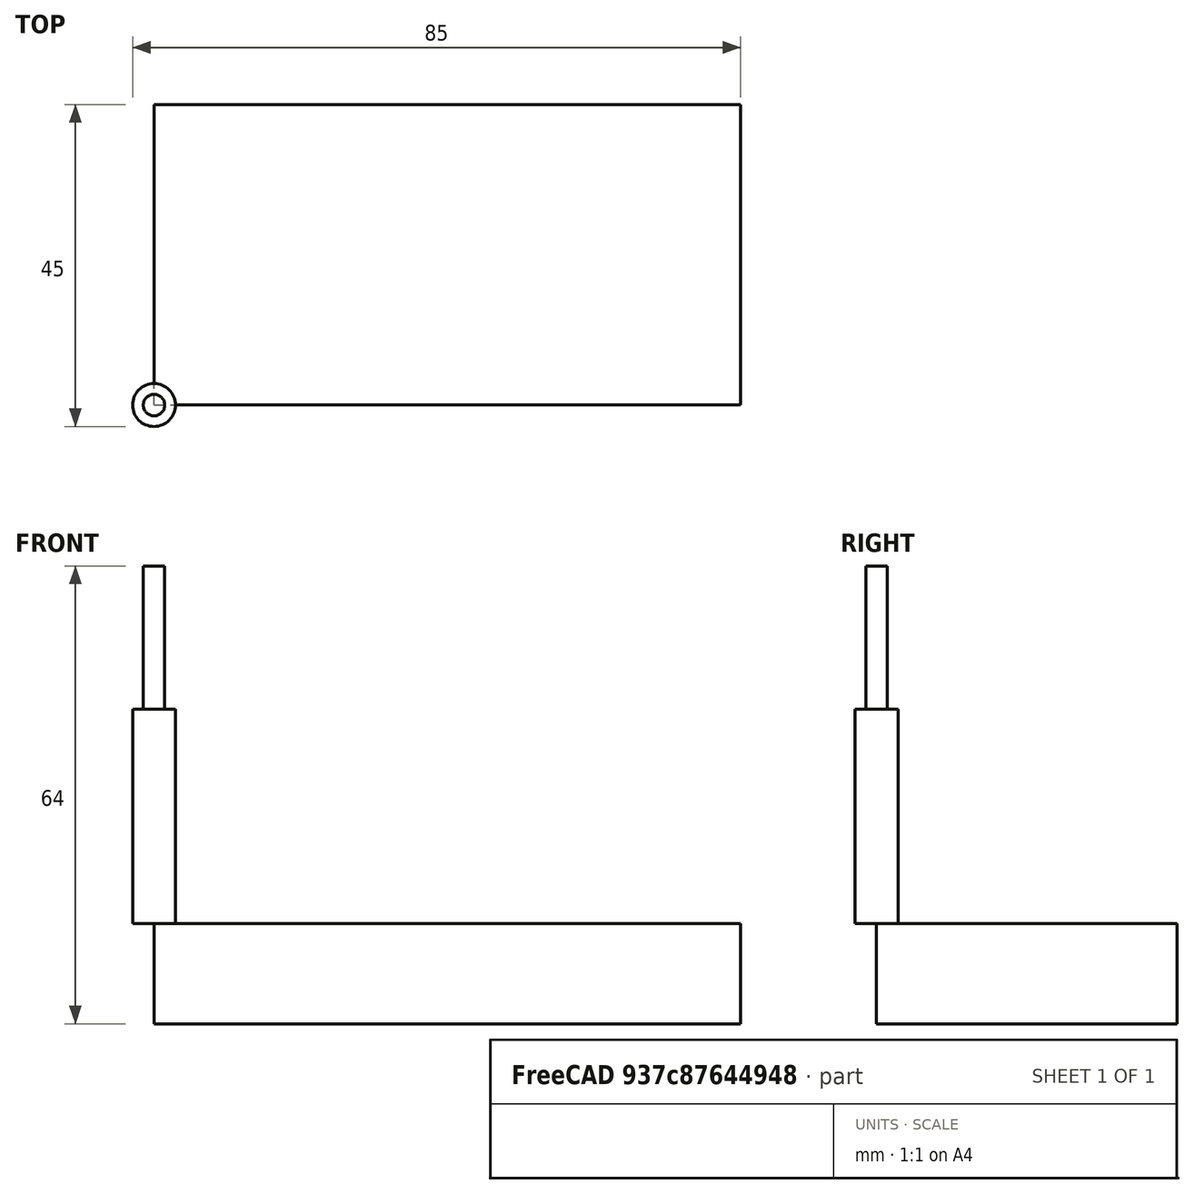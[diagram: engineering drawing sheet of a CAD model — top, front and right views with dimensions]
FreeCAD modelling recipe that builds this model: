
FCSTD DOCUMENT  (FreeCAD 0.19R23546 (Git))
Label: Cylindres
License: All rights reserved
LicenseURL: http://en.wikipedia.org/wiki/All_rights_reserved
objects: Path::FeaturePython×5, Sketcher::SketchObject×3, Part::FeaturePython×3, PartDesign::Pocket×2, PartDesign::Pad×1, App::FeaturePython×1, PartDesign::Body×1, App::DocumentObjectGroup×1, Path::FeatureCompoundPython×1, Mesh::FeaturePython×1
note: 15 computed .brp shape members not serialized (recipe doc carries the construction recipe); baked Part::Feature solids carry a one-line shape summary decoded from their .brp

FEATURE [Sketcher::SketchObject] Sketch
  MapMode = 5
  Support = -> [XY_Plane]
  sketch-geometry (4):
    g0: LineSegment StartX=0 StartY=40 StartZ=0 EndX=80 EndY=40 EndZ=0
    g1: LineSegment StartX=80 StartY=40 StartZ=0 EndX=80 EndY=0 EndZ=0
    g2: LineSegment StartX=80 StartY=0 StartZ=0 EndX=0 EndY=0 EndZ=0
    g3: LineSegment StartX=0 StartY=0 StartZ=0 EndX=0 EndY=40 EndZ=0
  constraints (9):
    c: Coincident(g0,g1)
    c: Coincident(g1,g2)
    c: Coincident(g2,g3)
    c: Coincident(g3,g0)
    c: Horizontal(g0)
    c: Horizontal(g2)
    c: Vertical(g1)
    c: Vertical(g3)
    c: PointOnObject(g0,g-2)
FEATURE [PartDesign::Pad] Pad
  Direction = (1,1,1)
  Length = 14
  Length2 = 100
  Profile = -> Sketch
  Type = 0
FEATURE [Sketcher::SketchObject] Sketch001
  MapMode = 5
  Placement = pos=(0,0,14) rot=(0,0,1;0rad)
  Support = -> [Pad]
  sketch-geometry (1):
    g0: Circle CenterX=20 CenterY=20 CenterZ=0 NormalX=0 NormalY=0 NormalZ=1 AngleXU=0 Radius=12.5
  constraints (1):
    c: Diameter(g0) = 25
FEATURE [PartDesign::Pocket] Pocket  label="Cylindre"
  BaseFeature = -> Pad
  Length = 5
  Length2 = 100
  Profile = -> Sketch001
  Type = 1
FEATURE [App::FeaturePython] SetupSheet  # Path/CAM operation (typed FeaturePython)
  ClearanceHeightExpression = OpStockZMax+SetupSheet.ClearanceHeightOffset
  ClearanceHeightOffset = 5
  CoolantMode = 0
  CoolantModes = None | Flood | Mist
  FinalDepthExpression = OpFinalDepth
  HorizRapid = 0
  SafeHeightExpression = OpStockZMax+SetupSheet.SafeHeightOffset
  SafeHeightOffset = 3
  StartDepthExpression = OpStartDepth
  StepDownExpression = OpToolDiameter
  VertRapid = 0
FEATURE [Part::FeaturePython] ToolBit  label="Endmill"  # Path/CAM toolbit (typed FeaturePython)
  BitShape = <path>
  CuttingEdgeHeight = 30
  Diameter = 6
  Length = 50
  ShankDiameter = 3
  ShapeName = endmill
FEATURE [Path::FeaturePython] TC__Default_Tool  label="TC: Default Tool"  # Path/CAM operation (typed FeaturePython)
  HorizFeed = 0
  HorizRapid = 0
  SpindleDir = 0
  SpindleSpeed = 0
  Tool = -> ToolBit
  ToolNumber = 1
  VertFeed = 0
  VertRapid = 0
  expr: HorizRapid = SetupSheet.HorizRapid
  expr: VertRapid = SetupSheet.VertRapid
FEATURE [Sketcher::SketchObject] Sketch002
  MapMode = 5
  Placement = pos=(0,0,14) rot=(0,0,1;0rad)
  Support = -> [Pocket]
  sketch-geometry (1):
    g0: Circle CenterX=60 CenterY=20 CenterZ=0 NormalX=0 NormalY=0 NormalZ=1 AngleXU=0 Radius=18.5
  constraints (1):
    c: Radius(g0) = 18.5
FEATURE [PartDesign::Pocket] Pocket001  label="Trou cylindrique"
  BaseFeature = -> Pocket
  Length = 5
  Length2 = 100
  Profile = -> Sketch002
  Type = 1
FEATURE [PartDesign::Body] Body
  Group = -> [Sketch,Pad,Sketch001,Pocket,Sketch002,Pocket001]
  Origin = -> Origin
  Tip = -> Pocket001
FEATURE [Part::FeaturePython] Clone  label="Model-Body"  # Draft clone (typed FeaturePython)
  AttacherType = Attacher::AttachEngine3D
  Fuse = false
  Objects = -> [Body]
  PathResource = Model
  Placement = pos=(1,1,-14) rot=(0,0,1;0rad)
  Scale = (1,1,1)
FEATURE [App::DocumentObjectGroup] Model
  Group = -> [Clone]
FEATURE [Part::FeaturePython] Stock  # WARN: FeaturePython — macro-defined, semantics opaque (R4)
  Base = -> Model
  ExtXneg = 1
  ExtXpos = 1
  ExtYneg = 1
  ExtYpos = 1
  ExtZneg = 0
  ExtZpos = 0
  Placement = pos=(1,1,-14) rot=(0,0,1;0rad)
  StockType = FromBase
FEATURE [Path::FeaturePython] Profile  # Path/CAM operation (typed FeaturePython)
  Active = true
  AreaParams:
    Tolerance = 1e-07
    FitArcs = True
    Simplify = False
    CleanDistance = 0.0
    Accuracy = 0.01
    Unit = 1.0
    MinArcPoints = 4
    MaxArcPoints = 100
    ClipperScale = 10000000.0
    Fill = 0
    Coplanar = 0
    Reorient = True
    Outline = False
    Explode = False
    OpenMode = 0
    Deflection = 0.01
    SubjectFill = 0
    ClipFill = 0
    Offset = -3.0
    ExtraPass = 0
    Stepover = 0.0
    LastStepover = 0.0
    JoinType = 0
    EndType = 0
    MiterLimit = 2.0
    RoundPrecision = 0.0
    PocketMode = 0
    ToolRadius = 1.0
    PocketExtraOffset = 0.0
    PocketStepover = 0.0
    PocketLastStepover = 0.0
    FromCenter = False
    Angle = 45.0
    AngleShift = 0.0
    Shift = 0.0
    Thicken = False
    SectionCount = -1
    Stepdown = 1.0
    SectionOffset = 0.0
    SectionTolerance = 1e-06
    SectionMode = 2
    Project = False
  AttemptInverseAngle = true
  Base = -> [Clone]
  ClearanceHeight = 5
  CoolantMode = None
  CycleTime = Erreur de temps de cycle
  Direction = 1
  EnableRotation = 0
  ExpandProfile = 0
  ExpandProfileStepOver = 100
  FinalDepth = -14
  HandleMultipleFeatures = 1
  InverseAngle = false
  JoinType = 0
  LimitDepthToFace = true
  MiterLimit = 0.1
  OffsetExtra = 0
  OpFinalDepth = -14
  OpStartDepth = 0
  OpStockZMax = 0
  OpStockZMin = -14
  OpToolDiameter = 6
  PathParams = {'orientation': 0, 'feedrate': 0.0, 'feedrate_v': 0.0, 'verbose': True, 'resume_height': 3.0, 'retraction': 5.0, 'return_end': True, 'preamble': False, 'start': Vector (0.0, 0.0, 0.0)}
  ReverseDirection = false
  SafeHeight = 3
  Side = 1
  StartDepth = 0
  StartPoint = (0,0,0)
  StepDown = 3
  ToolController = -> TC__Default_Tool
  UseComp = true
  UseStartPoint = true
  processCircles = false
  processHoles = false
  processPerimeter = true
  expr: ClearanceHeight = OpStockZMax + SetupSheet.ClearanceHeightOffset
  expr: SafeHeight = OpStockZMax + SetupSheet.SafeHeightOffset
  expr: StepDown = 3
  expr: FinalDepth = OpFinalDepth
  expr: StartDepth = OpStartDepth
FEATURE [Path::FeaturePython] Pocket_Shape  # Path/CAM operation (typed FeaturePython)
  Active = true
  AreaParams:
    Tolerance = 1e-07
    FitArcs = True
    Simplify = False
    CleanDistance = 0.0
    Accuracy = 0.01
    Unit = 1.0
    MinArcPoints = 4
    MaxArcPoints = 100
    ClipperScale = 10000000.0
    Fill = 0
    Coplanar = 0
    Reorient = True
    Outline = False
    Explode = False
    OpenMode = 0
    Deflection = 0.01
    SubjectFill = 0
    ClipFill = 0
    Offset = 0.0
    ExtraPass = 0
    Stepover = 0.0
    LastStepover = 0.0
    JoinType = 0
    EndType = 0
    MiterLimit = 2.0
    RoundPrecision = 0.0
    PocketMode = 4
    ToolRadius = 3.0
    PocketExtraOffset = 0.0
    PocketStepover = 6.0
    PocketLastStepover = 0.0
    FromCenter = True
    Angle = 45.0
    AngleShift = 0.0
    Shift = 0.0
    Thicken = False
    SectionCount = -1
    Stepdown = 1.0
    SectionOffset = 0.0
    SectionTolerance = 1e-06
    SectionMode = 2
    Project = False
  AttemptInverseAngle = true
  Base = -> [Clone]
  ClearanceHeight = 5
  CoolantMode = None
  CutMode = 0
  CycleTime = Erreur de temps de cycle
  EnableRotation = 0
  ExtensionCorners = true
  ExtensionLengthDefault = 3
  ExtraOffset = 0
  FinalDepth = -14
  FinishDepth = 0
  InverseAngle = false
  KeepToolDown = false
  LimitDepthToFace = true
  MinTravel = false
  OffsetPattern = 3
  OpFinalDepth = -14
  OpStartDepth = 0
  OpStockZMax = 0
  OpStockZMin = -14
  OpToolDiameter = 6
  PathParams = {'orientation': 1, 'feedrate': 0.0, 'feedrate_v': 0.0, 'verbose': True, 'resume_height': 3.0, 'retraction': 5.0, 'return_end': True, 'preamble': False}
  ReverseDirection = false
  SafeHeight = 3
  StartAt = 0
  StartDepth = 0
  StartPoint = (0,0,0)
  StepDown = 3
  StepOver = 100
  ToolController = -> TC__Default_Tool
  UseOutline = false
  UseStartPoint = false
  ZigZagAngle = 45
  expr: ExtensionLengthDefault = OpToolDiameter / 2
  expr: ClearanceHeight = OpStockZMax + SetupSheet.ClearanceHeightOffset
  expr: SafeHeight = OpStockZMax + SetupSheet.SafeHeightOffset
  expr: StepDown = 3
  expr: FinalDepth = -14
  expr: StartDepth = 0
FEATURE [Path::FeaturePython] DressupTag  # Path/CAM operation (typed FeaturePython)
  Angle = 45
  Base = -> Profile
  Height = 7
  Positions = (4) [(47.8211,29.1559,0),(52.8441,7.82115,0),(73.2957,11.5652,0),(70.4348,33.2957,0)]
  Radius = 0
  SegmentationFactor = 50
  Width = 2.75
FEATURE [Path::FeatureCompoundPython] Operations  # Path/CAM operation (typed FeaturePython)
  Group = -> [DressupTag,Pocket_Shape]
  UsePlacements = false
FEATURE [Path::FeaturePython] Job  # Path/CAM operation (typed FeaturePython)
  CycleTime = 00:00:00
  Fixtures = G54
  GeometryTolerance = 0.01
  LastPostProcessDate = 2021-04-13 11:13:49.805593
  LastPostProcessOutput = <userpath>/dev/CNC/MiscCNC/FixationsCNC/Cylindres.gcode
  Model = -> Model
  Operations = -> Operations
  OrderOutputBy = 0
  PostProcessor = 13
  PostProcessorOutputFile = <userpath>/dev/CNC/MiscCNC/FixationsCNC/Cylindres.gcode
  SetupSheet = -> SetupSheet
  SplitOutput = false
  Stock = -> Stock
  ToolController = -> [TC__Default_Tool]
FEATURE [Mesh::FeaturePython] CutMaterial  # WARN: FeaturePython — macro-defined, semantics opaque (R4)
note: 1 file-system path scrubbed to <path> (originals preserved in the JSON sidecar)
